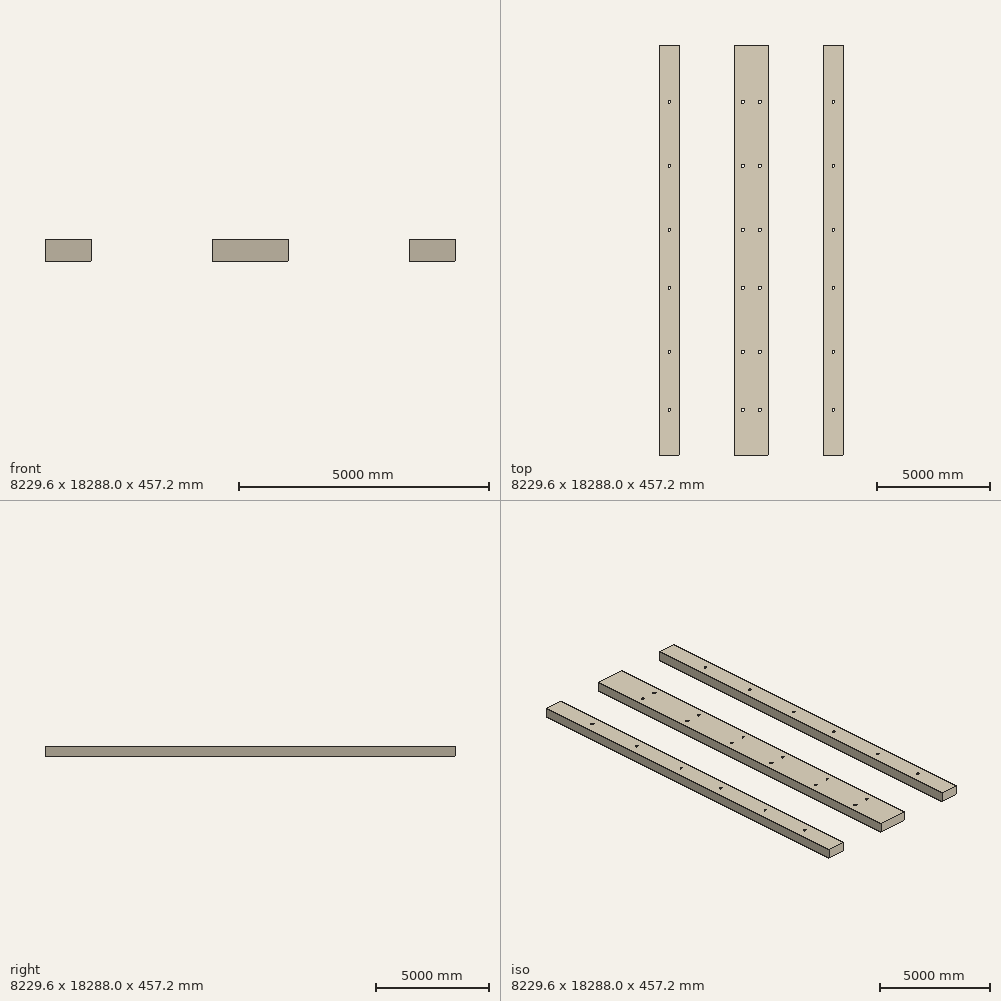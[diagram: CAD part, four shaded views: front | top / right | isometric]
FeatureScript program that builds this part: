
annotation { "Feature Type Name" : "Feature", "Feature Type Description" : "" }
export const myFeature = defineFeature(function(context is Context, id is Id, definition is map)
    precondition{}
    {
        {
            var Q0;
            Q0=qCreatedBy(makeId("Top.planeOp"),FACE);
            var sketch = newSketch(context, id + "F0", { "sketchPlane" : qUnion([Q0])});
            skLineSegment(sketch, "E0.bottom", {"start": v(-4114.8, 9144) * mm, "end": v(-3200.4, 9144) * mm});
            skLineSegment(sketch, "E0.top", {"start": v(-4114.8, -9144) * mm, "end": v(-3200.4, -9144) * mm});
            skLineSegment(sketch, "E0.left", {"start": v(-4114.8, 9144) * mm, "end": v(-4114.8, -9144) * mm});
            skLineSegment(sketch, "E0.right", {"start": v(-3200.4, 9144) * mm, "end": v(-3200.4, -9144) * mm});
            skLineSegment(sketch, "E1.bottom", {"start": v(-762, 9144) * mm, "end": v(0, 9144) * mm});
            skLineSegment(sketch, "E1.top", {"start": v(-762, -9144) * mm, "end": v(0, -9144) * mm});
            skLineSegment(sketch, "E1.left", {"start": v(-762, 9144) * mm, "end": v(-762, -9144) * mm});
            skLineSegment(sketch, "E1.right", {"start": v(0, 9144) * mm, "end": v(0, -9144) * mm});
            skLineSegment(sketch, "E2.bottom", {"start": v(0, 9144) * mm, "end": v(762, 9144) * mm});
            skLineSegment(sketch, "E2.top", {"start": v(0, -9144) * mm, "end": v(762, -9144) * mm});
            skLineSegment(sketch, "E2.right", {"start": v(762, 9144) * mm, "end": v(762, -9144) * mm});
            skLineSegment(sketch, "E3.bottom", {"start": v(3200.4, 9144) * mm, "end": v(4114.8, 9144) * mm});
            skLineSegment(sketch, "E3.top", {"start": v(3200.4, -9144) * mm, "end": v(4114.8, -9144) * mm});
            skLineSegment(sketch, "E3.left", {"start": v(3200.4, 9144) * mm, "end": v(3200.4, -9144) * mm});
            skLineSegment(sketch, "E3.right", {"start": v(4114.8, 9144) * mm, "end": v(4114.8, -9144) * mm});
            skLineSegment(sketch, "E4.bottom", {"start": v(-3594.1, 6705.6) * mm, "end": v(-3721.1, 6705.6) * mm});
            skLineSegment(sketch, "E4.top", {"start": v(-3594.1, 6578.6) * mm, "end": v(-3721.1, 6578.6) * mm});
            skLineSegment(sketch, "E4.left", {"start": v(-3594.1, 6705.6) * mm, "end": v(-3594.1, 6578.6) * mm});
            skLineSegment(sketch, "E4.right", {"start": v(-3721.1, 6705.6) * mm, "end": v(-3721.1, 6578.6) * mm});
            skPoint(sketch, "E4.middle", {"position": v(-3657.6, 6642.1) * mm});
            skPoint(sketch, "E5", {"position": v(-3657.6, 9144) * mm});
            skLineSegment(sketch, "E6.bottom", {"start": v(-3594.1, 3835.4) * mm, "end": v(-3721.1, 3835.4) * mm});
            skLineSegment(sketch, "E6.top", {"start": v(-3594.1, 3708.4) * mm, "end": v(-3721.1, 3708.4) * mm});
            skLineSegment(sketch, "E6.left", {"start": v(-3721.1, 3835.4) * mm, "end": v(-3721.1, 3708.4) * mm});
            skLineSegment(sketch, "E6.right", {"start": v(-3594.1, 3835.4) * mm, "end": v(-3594.1, 3708.4) * mm});
            skPoint(sketch, "E6.middle", {"position": v(-3657.6, 3771.9) * mm});
            skLineSegment(sketch, "E7.bottom", {"start": v(-3594.1, -1600.2) * mm, "end": v(-3721.1, -1600.2) * mm});
            skLineSegment(sketch, "E7.top", {"start": v(-3594.1, -1727.2) * mm, "end": v(-3721.1, -1727.2) * mm});
            skLineSegment(sketch, "E7.left", {"start": v(-3594.1, -1600.2) * mm, "end": v(-3594.1, -1727.2) * mm});
            skLineSegment(sketch, "E7.right", {"start": v(-3721.1, -1600.2) * mm, "end": v(-3721.1, -1727.2) * mm});
            skPoint(sketch, "E7.middle", {"position": v(-3657.6, -1663.7) * mm});
            skLineSegment(sketch, "E8.bottom", {"start": v(-3594.1, -4470.4) * mm, "end": v(-3721.1, -4470.4) * mm});
            skLineSegment(sketch, "E8.top", {"start": v(-3594.1, -4597.4) * mm, "end": v(-3721.1, -4597.4) * mm});
            skLineSegment(sketch, "E8.left", {"start": v(-3594.1, -4470.4) * mm, "end": v(-3594.1, -4597.4) * mm});
            skLineSegment(sketch, "E8.right", {"start": v(-3721.1, -4470.4) * mm, "end": v(-3721.1, -4597.4) * mm});
            skPoint(sketch, "E8.middle", {"position": v(-3657.6, -4533.9) * mm});
            skLineSegment(sketch, "E9.bottom", {"start": v(-3594.1, 965.2) * mm, "end": v(-3721.1, 965.2) * mm});
            skLineSegment(sketch, "E9.top", {"start": v(-3594.1, 838.2) * mm, "end": v(-3721.1, 838.2) * mm});
            skLineSegment(sketch, "E9.left", {"start": v(-3594.1, 965.2) * mm, "end": v(-3594.1, 838.2) * mm});
            skLineSegment(sketch, "E9.right", {"start": v(-3721.1, 965.2) * mm, "end": v(-3721.1, 838.2) * mm});
            skPoint(sketch, "E9.middle", {"position": v(-3657.6, 901.7) * mm});
            skLineSegment(sketch, "E10.bottom", {"start": v(-3594.1, -7035.8) * mm, "end": v(-3721.1, -7035.8) * mm});
            skLineSegment(sketch, "E10.top", {"start": v(-3594.1, -7162.8) * mm, "end": v(-3721.1, -7162.8) * mm});
            skLineSegment(sketch, "E10.left", {"start": v(-3594.1, -7035.8) * mm, "end": v(-3594.1, -7162.8) * mm});
            skLineSegment(sketch, "E10.right", {"start": v(-3721.1, -7035.8) * mm, "end": v(-3721.1, -7162.8) * mm});
            skPoint(sketch, "E10.middle", {"position": v(-3657.6, -7099.3) * mm});
            skPoint(sketch, "E11", {"position": v(-3657.6, -1727.2) * mm});
            skPoint(sketch, "E12", {"position": v(-3657.6, -7162.8) * mm});
            skPoint(sketch, "E13", {"position": v(-3657.6, -4597.4) * mm});
            skLineSegment(sketch, "E14.1.0.0", {"start": v(-317.5, 6705.6) * mm, "end": v(-444.5, 6705.6) * mm});
            skLineSegment(sketch, "E14.1.0.1", {"start": v(-444.5, 6705.6) * mm, "end": v(-444.5, 6578.6) * mm});
            skLineSegment(sketch, "E14.1.0.2", {"start": v(-317.5, 6705.6) * mm, "end": v(-317.5, 6578.6) * mm});
            skLineSegment(sketch, "E14.1.0.3", {"start": v(-317.5, 6578.6) * mm, "end": v(-444.5, 6578.6) * mm});
            skPoint(sketch, "E14.1.0.4", {"position": v(-381, 6642.1) * mm});
            skPoint(sketch, "E14.1.0.5", {"position": v(-381, -7099.3) * mm});
            skPoint(sketch, "E14.1.0.6", {"position": v(-381, 901.7) * mm});
            skPoint(sketch, "E14.1.0.7", {"position": v(-381, -1663.7) * mm});
            skPoint(sketch, "E14.1.0.8", {"position": v(-381, -1727.2) * mm});
            skPoint(sketch, "E14.1.0.9", {"position": v(-381, -4533.9) * mm});
            skPoint(sketch, "E14.1.0.10", {"position": v(-381, -7162.8) * mm});
            skPoint(sketch, "E14.1.0.11", {"position": v(-381, 3771.9) * mm});
            skPoint(sketch, "E14.1.0.12", {"position": v(-381, -4597.4) * mm});
            skLineSegment(sketch, "E14.1.0.13", {"start": v(-317.5, 3835.4) * mm, "end": v(-317.5, 3708.4) * mm});
            skLineSegment(sketch, "E14.1.0.14", {"start": v(-444.5, -7035.8) * mm, "end": v(-444.5, -7162.8) * mm});
            skLineSegment(sketch, "E14.1.0.15", {"start": v(-317.5, -4470.4) * mm, "end": v(-444.5, -4470.4) * mm});
            skLineSegment(sketch, "E14.1.0.16", {"start": v(-317.5, 3835.4) * mm, "end": v(-444.5, 3835.4) * mm});
            skLineSegment(sketch, "E14.1.0.17", {"start": v(-317.5, -1600.2) * mm, "end": v(-317.5, -1727.2) * mm});
            skLineSegment(sketch, "E14.1.0.18", {"start": v(-444.5, 965.2) * mm, "end": v(-444.5, 838.2) * mm});
            skLineSegment(sketch, "E14.1.0.19", {"start": v(-317.5, -1727.2) * mm, "end": v(-444.5, -1727.2) * mm});
            skLineSegment(sketch, "E14.1.0.20", {"start": v(-317.5, 965.2) * mm, "end": v(-444.5, 965.2) * mm});
            skLineSegment(sketch, "E14.1.0.21", {"start": v(-444.5, -4470.4) * mm, "end": v(-444.5, -4597.4) * mm});
            skLineSegment(sketch, "E14.1.0.22", {"start": v(-317.5, -7035.8) * mm, "end": v(-317.5, -7162.8) * mm});
            skLineSegment(sketch, "E14.1.0.23", {"start": v(-317.5, 838.2) * mm, "end": v(-444.5, 838.2) * mm});
            skLineSegment(sketch, "E14.1.0.24", {"start": v(-317.5, 965.2) * mm, "end": v(-317.5, 838.2) * mm});
            skLineSegment(sketch, "E14.1.0.25", {"start": v(-444.5, -1600.2) * mm, "end": v(-444.5, -1727.2) * mm});
            skLineSegment(sketch, "E14.1.0.26", {"start": v(-317.5, -1600.2) * mm, "end": v(-444.5, -1600.2) * mm});
            skLineSegment(sketch, "E14.1.0.27", {"start": v(-317.5, -7035.8) * mm, "end": v(-444.5, -7035.8) * mm});
            skLineSegment(sketch, "E14.1.0.28", {"start": v(-317.5, -7162.8) * mm, "end": v(-444.5, -7162.8) * mm});
            skLineSegment(sketch, "E14.1.0.29", {"start": v(-317.5, -4597.4) * mm, "end": v(-444.5, -4597.4) * mm});
            skLineSegment(sketch, "E14.1.0.30", {"start": v(-444.5, 3835.4) * mm, "end": v(-444.5, 3708.4) * mm});
            skLineSegment(sketch, "E14.1.0.31", {"start": v(-317.5, 3708.4) * mm, "end": v(-444.5, 3708.4) * mm});
            skLineSegment(sketch, "E14.1.0.32", {"start": v(-317.5, -4470.4) * mm, "end": v(-317.5, -4597.4) * mm});
            skLineSegment(sketch, "E14.direction1", {"start": v(-3721.1, -7162.8) * mm, "end": v(-444.5, -7162.8) * mm, "construction": true});
            skPoint(sketch, "E15", {"position": v(-381, 9144) * mm});
            skLineSegment(sketch, "E16.MirrorCS", {"start": v(317.5, -7162.8) * mm, "end": v(444.5, -7162.8) * mm});
            skLineSegment(sketch, "E17.MirrorCS", {"start": v(3721.1, -7035.8) * mm, "end": v(3721.1, -7162.8) * mm});
            skLineSegment(sketch, "E18.MirrorCS", {"start": v(3721.1, -1600.2) * mm, "end": v(3721.1, -1727.2) * mm});
            skLineSegment(sketch, "E19.MirrorCS", {"start": v(317.5, 6578.6) * mm, "end": v(444.5, 6578.6) * mm});
            skLineSegment(sketch, "E20.MirrorCS", {"start": v(317.5, -1600.2) * mm, "end": v(444.5, -1600.2) * mm});
            skLineSegment(sketch, "E21.MirrorCS", {"start": v(3594.1, 3835.4) * mm, "end": v(3594.1, 3708.4) * mm});
            skLineSegment(sketch, "E22.MirrorCS", {"start": v(317.5, 965.2) * mm, "end": v(317.5, 838.2) * mm});
            skLineSegment(sketch, "E23.MirrorCS", {"start": v(444.5, -7035.8) * mm, "end": v(444.5, -7162.8) * mm});
            skLineSegment(sketch, "E24.MirrorCS", {"start": v(444.5, -4470.4) * mm, "end": v(444.5, -4597.4) * mm});
            skLineSegment(sketch, "E25.MirrorCS", {"start": v(3594.1, -7035.8) * mm, "end": v(3721.1, -7035.8) * mm});
            skLineSegment(sketch, "E26.MirrorCS", {"start": v(3594.1, -4597.4) * mm, "end": v(3721.1, -4597.4) * mm});
            skLineSegment(sketch, "E27.MirrorCS", {"start": v(444.5, 3835.4) * mm, "end": v(444.5, 3708.4) * mm});
            skLineSegment(sketch, "E28.MirrorCS", {"start": v(317.5, -1727.2) * mm, "end": v(444.5, -1727.2) * mm});
            skLineSegment(sketch, "E29.MirrorCS", {"start": v(3594.1, 965.2) * mm, "end": v(3594.1, 838.2) * mm});
            skLineSegment(sketch, "E30.MirrorCS", {"start": v(3594.1, 6705.6) * mm, "end": v(3594.1, 6578.6) * mm});
            skLineSegment(sketch, "E31.MirrorCS", {"start": v(317.5, 3835.4) * mm, "end": v(317.5, 3708.4) * mm});
            skLineSegment(sketch, "E32.MirrorCS", {"start": v(317.5, -7035.8) * mm, "end": v(317.5, -7162.8) * mm});
            skLineSegment(sketch, "E33.MirrorCS", {"start": v(3594.1, -7162.8) * mm, "end": v(3721.1, -7162.8) * mm});
            skLineSegment(sketch, "E34.MirrorCS", {"start": v(317.5, -7035.8) * mm, "end": v(444.5, -7035.8) * mm});
            skLineSegment(sketch, "E35.MirrorCS", {"start": v(3594.1, -4470.4) * mm, "end": v(3721.1, -4470.4) * mm});
            skLineSegment(sketch, "E36.MirrorCS", {"start": v(3594.1, -7035.8) * mm, "end": v(3594.1, -7162.8) * mm});
            skLineSegment(sketch, "E37.MirrorCS", {"start": v(444.5, 965.2) * mm, "end": v(444.5, 838.2) * mm});
            skLineSegment(sketch, "E38.MirrorCS", {"start": v(3594.1, 838.2) * mm, "end": v(3721.1, 838.2) * mm});
            skLineSegment(sketch, "E39.MirrorCS", {"start": v(3594.1, 6578.6) * mm, "end": v(3721.1, 6578.6) * mm});
            skLineSegment(sketch, "E40.MirrorCS", {"start": v(3594.1, -1727.2) * mm, "end": v(3721.1, -1727.2) * mm});
            skLineSegment(sketch, "E41.MirrorCS", {"start": v(444.5, 6705.6) * mm, "end": v(444.5, 6578.6) * mm});
            skLineSegment(sketch, "E42.MirrorCS", {"start": v(3721.1, 965.2) * mm, "end": v(3721.1, 838.2) * mm});
            skLineSegment(sketch, "E43.MirrorCS", {"start": v(3721.1, -4470.4) * mm, "end": v(3721.1, -4597.4) * mm});
            skLineSegment(sketch, "E44.MirrorCS", {"start": v(317.5, 965.2) * mm, "end": v(444.5, 965.2) * mm});
            skLineSegment(sketch, "E45.MirrorCS", {"start": v(3594.1, 3835.4) * mm, "end": v(3721.1, 3835.4) * mm});
            skLineSegment(sketch, "E46.MirrorCS", {"start": v(317.5, -1600.2) * mm, "end": v(317.5, -1727.2) * mm});
            skLineSegment(sketch, "E47.MirrorCS", {"start": v(3594.1, 965.2) * mm, "end": v(3721.1, 965.2) * mm});
            skLineSegment(sketch, "E48.MirrorCS", {"start": v(3594.1, 6705.6) * mm, "end": v(3721.1, 6705.6) * mm});
            skLineSegment(sketch, "E49.MirrorCS", {"start": v(317.5, 6705.6) * mm, "end": v(317.5, 6578.6) * mm});
            skLineSegment(sketch, "E50.MirrorCS", {"start": v(3594.1, 3708.4) * mm, "end": v(3721.1, 3708.4) * mm});
            skLineSegment(sketch, "E51.MirrorCS", {"start": v(3721.1, 6705.6) * mm, "end": v(3721.1, 6578.6) * mm});
            skLineSegment(sketch, "E52.MirrorCS", {"start": v(317.5, 3835.4) * mm, "end": v(444.5, 3835.4) * mm});
            skLineSegment(sketch, "E53.MirrorCS", {"start": v(3594.1, -1600.2) * mm, "end": v(3594.1, -1727.2) * mm});
            skLineSegment(sketch, "E54.MirrorCS", {"start": v(3594.1, -4470.4) * mm, "end": v(3594.1, -4597.4) * mm});
            skLineSegment(sketch, "E55.MirrorCS", {"start": v(444.5, -1600.2) * mm, "end": v(444.5, -1727.2) * mm});
            skLineSegment(sketch, "E56.MirrorCS", {"start": v(3721.1, 3835.4) * mm, "end": v(3721.1, 3708.4) * mm});
            skLineSegment(sketch, "E57.MirrorCS", {"start": v(3594.1, -1600.2) * mm, "end": v(3721.1, -1600.2) * mm});
            skLineSegment(sketch, "E58.MirrorCS", {"start": v(317.5, -4470.4) * mm, "end": v(444.5, -4470.4) * mm});
            skLineSegment(sketch, "E59.MirrorCS", {"start": v(317.5, -4470.4) * mm, "end": v(317.5, -4597.4) * mm});
            skLineSegment(sketch, "E60.MirrorCS", {"start": v(317.5, -4597.4) * mm, "end": v(444.5, -4597.4) * mm});
            skLineSegment(sketch, "E61.MirrorCS", {"start": v(317.5, 838.2) * mm, "end": v(444.5, 838.2) * mm});
            skLineSegment(sketch, "E62.MirrorCS", {"start": v(317.5, 3708.4) * mm, "end": v(444.5, 3708.4) * mm});
            skLineSegment(sketch, "E63.MirrorCS", {"start": v(317.5, 6705.6) * mm, "end": v(444.5, 6705.6) * mm});
            skPoint(sketch, "E64.MirrorP", {"position": v(381, 6642.1) * mm});
            skPoint(sketch, "E65.MirrorP", {"position": v(3657.6, -7162.8) * mm});
            skPoint(sketch, "E66.MirrorP", {"position": v(3657.6, 6642.1) * mm});
            skPoint(sketch, "E67.MirrorP", {"position": v(381, -7162.8) * mm});
            skPoint(sketch, "E68.MirrorP", {"position": v(3657.6, -7099.3) * mm});
            skPoint(sketch, "E69.MirrorP", {"position": v(381, 901.7) * mm});
            skPoint(sketch, "E70.MirrorP", {"position": v(3657.6, -1663.7) * mm});
            skPoint(sketch, "E71.MirrorP", {"position": v(381, 3771.9) * mm});
            skPoint(sketch, "E72.MirrorP", {"position": v(381, -4533.9) * mm});
            skLineSegment(sketch, "E73.MirrorCS", {"start": v(3721.1, -7162.8) * mm, "end": v(444.5, -7162.8) * mm, "construction": true});
            skPoint(sketch, "E74.MirrorP", {"position": v(381, -4597.4) * mm});
            skPoint(sketch, "E75.MirrorP", {"position": v(381, -1663.7) * mm});
            skPoint(sketch, "E76.MirrorP", {"position": v(3657.6, -4597.4) * mm});
            skPoint(sketch, "E77.MirrorP", {"position": v(381, -7099.3) * mm});
            skPoint(sketch, "E78.MirrorP", {"position": v(381, -1727.2) * mm});
            skPoint(sketch, "E79.MirrorP", {"position": v(3657.6, 901.7) * mm});
            skPoint(sketch, "E80.MirrorP", {"position": v(3657.6, 3771.9) * mm});
            skPoint(sketch, "E81.MirrorP", {"position": v(3657.6, -4533.9) * mm});
            skPoint(sketch, "E82.MirrorP", {"position": v(3657.6, -1727.2) * mm});
            skSolve(sketch);
        }
        {
            var Q0;
            Q0=makeQuery(id+"F0.imprint","IMPRINT",FACE,{"disambiguationData":[TD([[makeQuery(id+"F0.imprint","IMPRINT",EDGE,{"derivedFrom":sQuery(id+"F0.wireOp",EDGE,"E0.bottom")}),-1.0]])]});
            var Q1;
            Q1=makeQuery(id+"F0.imprint","IMPRINT",FACE,{"disambiguationData":[TD([[makeQuery(id+"F0.imprint","IMPRINT",EDGE,{"derivedFrom":sQuery(id+"F0.wireOp",EDGE,"E1.bottom")}),-1.0]])]});
            extrude(context, id + "F1", {"entities" : qUnion([Q0, Q1]), "depth" : 457.2 * mm, "offsetDistance" : 30.48 * mm});
        }
        {
            var Q0;
            Q0=makeQuery(id+"F1.opExtrude","SWEPT_BODY",BODY,{"disambiguationData":[OSD([sQuery(id+"F0.wireOp",EDGE,"E0.bottom"),sQuery(id+"F0.wireOp",EDGE,"E0.top"),sQuery(id+"F0.wireOp",EDGE,"E0.left"),sQuery(id+"F0.wireOp",EDGE,"E0.right"),sQuery(id+"F0.wireOp",EDGE,"E4.bottom"),sQuery(id+"F0.wireOp",EDGE,"E4.top"),sQuery(id+"F0.wireOp",EDGE,"E4.left"),sQuery(id+"F0.wireOp",EDGE,"E4.right"),sQuery(id+"F0.wireOp",EDGE,"E6.bottom"),sQuery(id+"F0.wireOp",EDGE,"E6.top"),sQuery(id+"F0.wireOp",EDGE,"E6.left"),sQuery(id+"F0.wireOp",EDGE,"E6.right"),sQuery(id+"F0.wireOp",EDGE,"E7.bottom"),sQuery(id+"F0.wireOp",EDGE,"E7.top"),sQuery(id+"F0.wireOp",EDGE,"E7.left"),sQuery(id+"F0.wireOp",EDGE,"E7.right"),sQuery(id+"F0.wireOp",EDGE,"E8.bottom"),sQuery(id+"F0.wireOp",EDGE,"E8.top"),sQuery(id+"F0.wireOp",EDGE,"E8.left"),sQuery(id+"F0.wireOp",EDGE,"E8.right"),sQuery(id+"F0.wireOp",EDGE,"E9.bottom"),sQuery(id+"F0.wireOp",EDGE,"E9.top"),sQuery(id+"F0.wireOp",EDGE,"E9.left"),sQuery(id+"F0.wireOp",EDGE,"E9.right"),sQuery(id+"F0.wireOp",EDGE,"E10.bottom"),sQuery(id+"F0.wireOp",EDGE,"E10.top"),sQuery(id+"F0.wireOp",EDGE,"E10.left"),sQuery(id+"F0.wireOp",EDGE,"E10.right")])]});
            var Q1;
            Q1=makeQuery(id+"F1.opExtrude","SWEPT_BODY",BODY,{"disambiguationData":[OSD([sQuery(id+"F0.wireOp",EDGE,"E1.bottom"),sQuery(id+"F0.wireOp",EDGE,"E1.top"),sQuery(id+"F0.wireOp",EDGE,"E1.left"),sQuery(id+"F0.wireOp",EDGE,"E1.right"),sQuery(id+"F0.wireOp",EDGE,"E14.1.0.0"),sQuery(id+"F0.wireOp",EDGE,"E14.1.0.1"),sQuery(id+"F0.wireOp",EDGE,"E14.1.0.2"),sQuery(id+"F0.wireOp",EDGE,"E14.1.0.3"),sQuery(id+"F0.wireOp",EDGE,"E14.1.0.13"),sQuery(id+"F0.wireOp",EDGE,"E14.1.0.14"),sQuery(id+"F0.wireOp",EDGE,"E14.1.0.15"),sQuery(id+"F0.wireOp",EDGE,"E14.1.0.16"),sQuery(id+"F0.wireOp",EDGE,"E14.1.0.17"),sQuery(id+"F0.wireOp",EDGE,"E14.1.0.18"),sQuery(id+"F0.wireOp",EDGE,"E14.1.0.19"),sQuery(id+"F0.wireOp",EDGE,"E14.1.0.20"),sQuery(id+"F0.wireOp",EDGE,"E14.1.0.21"),sQuery(id+"F0.wireOp",EDGE,"E14.1.0.22"),sQuery(id+"F0.wireOp",EDGE,"E14.1.0.23"),sQuery(id+"F0.wireOp",EDGE,"E14.1.0.24"),sQuery(id+"F0.wireOp",EDGE,"E14.1.0.25"),sQuery(id+"F0.wireOp",EDGE,"E14.1.0.26"),sQuery(id+"F0.wireOp",EDGE,"E14.1.0.27"),sQuery(id+"F0.wireOp",EDGE,"E14.1.0.28"),sQuery(id+"F0.wireOp",EDGE,"E14.1.0.29"),sQuery(id+"F0.wireOp",EDGE,"E14.1.0.30"),sQuery(id+"F0.wireOp",EDGE,"E14.1.0.31"),sQuery(id+"F0.wireOp",EDGE,"E14.1.0.32")])]});
            var Q2;
            Q2=qCreatedBy(makeId("Right.planeOp"),FACE);
            mirror(context, id + "F2", {"operationType" : NewBodyOperationType.ADD, "entities" : qUnion([Q0, Q1]), "mirrorPlane" : qUnion([Q2])});
        }
    });
